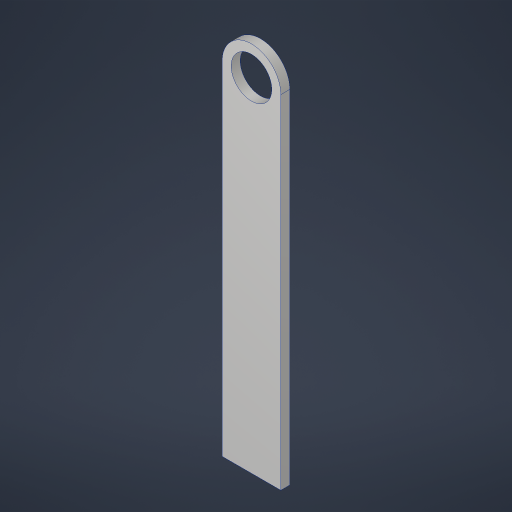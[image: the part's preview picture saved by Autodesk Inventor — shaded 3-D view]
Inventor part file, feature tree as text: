
AUTODESK INVENTOR PART (.ipt)
format: ipt  version: 2023.4 (Build 274418000, 418)  size: 171,520 bytes
history: native  units: in
note: dims shown in document units (in); Inventor stores cm internally (conversion verified against a paired STEP export)
features: extrude x1, sketch x1
ambient origin geometry x8: Origin, YZ Plane, XZ Plane, XY Plane, X Axis, Y Axis, Z Axis, Center Point
bodies: Solid1 (feature_tree)
feature tree (2):
  extrude  "Extrusion1"  Depth=0.25in
  sketch  "Sketch1"  dims[d0=1.125in d1=0.25in d2=9.5in d3=0.25in d4=0.0in]
